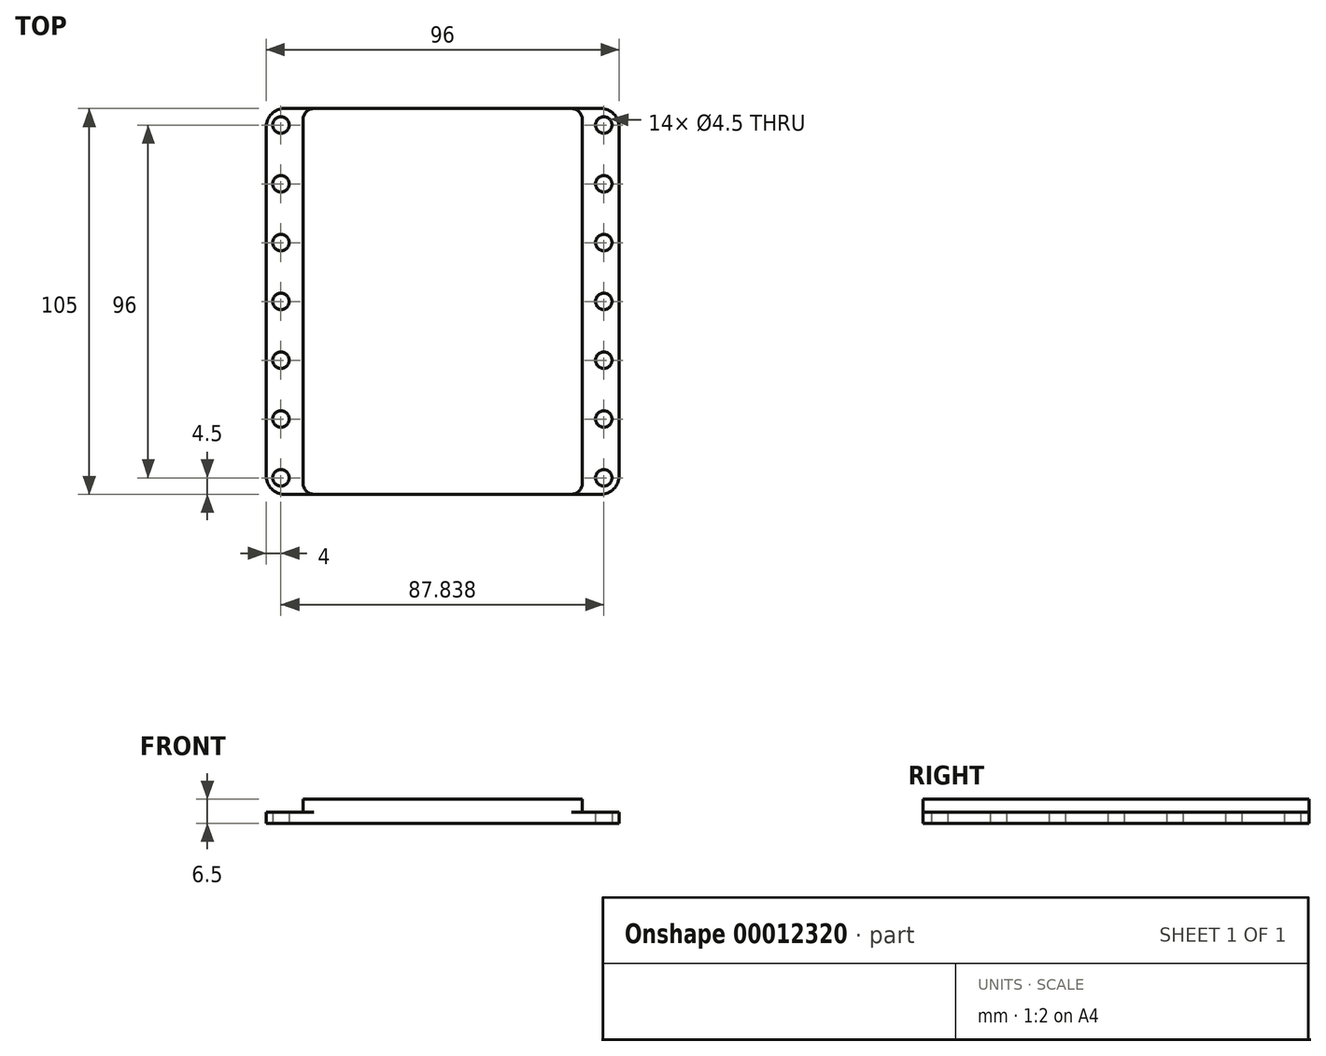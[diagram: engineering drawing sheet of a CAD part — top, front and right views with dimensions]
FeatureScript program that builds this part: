
annotation { "Feature Type Name" : "Feature", "Feature Type Description" : "" }
export const myFeature = defineFeature(function(context is Context, id is Id, definition is map)
    precondition{}
    {
        {
            var Q0;
            Q0=qCreatedBy(makeId("Front.planeOp"),FACE);
            var sketch = newSketch(context, id + "F0", { "sketchPlane" : qUnion([Q0])});
            skLineSegment(sketch, "E0.bottom", {"start": v(0, 0) * mm, "end": v(96, 0) * mm});
            skLineSegment(sketch, "E0.top", {"start": v(0, 3) * mm, "end": v(10, 3) * mm});
            skLineSegment(sketch, "E0.left", {"start": v(0, 0) * mm, "end": v(0, 3) * mm});
            skLineSegment(sketch, "E0.right", {"start": v(96, 0) * mm, "end": v(96, 3) * mm});
            skLineSegment(sketch, "E1.rect.bottom", {"start": v(86, 6.5) * mm, "end": v(10, 6.5) * mm});
            skLineSegment(sketch, "E1.rect.left", {"start": v(86, 6.5) * mm, "end": v(86, 3) * mm});
            skLineSegment(sketch, "E1.rect.right", {"start": v(10, 6.5) * mm, "end": v(10, 3) * mm});
            skPoint(sketch, "E1.rect.middle", {"position": v(48, 3) * mm});
            skLineSegment(sketch, "E2.trimOffspring", {"start": v(86, 3) * mm, "end": v(96, 3) * mm});
            skPoint(sketch, "E3.orphan", {"position": v(86, -0.5) * mm});
            skPoint(sketch, "E4.orphan", {"position": v(10, -0.5) * mm});
            skSolve(sketch);
        }
        {
            var Q0;
            Q0=qSketchRegion(id+"F0",true);
            extrude(context, id + "F1", {"entities" : qUnion([Q0]), "depth" : 105 * mm});
        }
        {
            var Q0;
            Q0=makeQuery(id+"F1.opExtrude","CAP_EDGE",EDGE,{"disambiguationData":[OSD([sQuery(id+"F0.wireOp",EDGE,"E1.rect.left")])],"isStart":false});
            var Q1;
            Q1=makeQuery(id+"F1.opExtrude","CAP_EDGE",EDGE,{"disambiguationData":[OSD([sQuery(id+"F0.wireOp",EDGE,"E1.rect.left")])],"isStart":true});
            var Q2;
            Q2=makeQuery(id+"F1.opExtrude","CAP_EDGE",EDGE,{"disambiguationData":[OSD([sQuery(id+"F0.wireOp",EDGE,"E1.rect.right")])],"isStart":false});
            var Q3;
            Q3=makeQuery(id+"F1.opExtrude","CAP_EDGE",EDGE,{"disambiguationData":[OSD([sQuery(id+"F0.wireOp",EDGE,"E1.rect.right")])],"isStart":true});
            fillet(context, id + "F2", {"entities" : qUnion([Q0, Q1, Q2, Q3]), "radius" : 3 * mm, "tangentPropagation" : true, "allowEdgeOverflow" : false});
        }
        {
            var Q0;
            Q0=makeQuery(id+"F1.opExtrude","CAP_EDGE",EDGE,{"disambiguationData":[OSD([sQuery(id+"F0.wireOp",EDGE,"E0.left")])],"isStart":true});
            var Q1;
            Q1=makeQuery(id+"F1.opExtrude","CAP_EDGE",EDGE,{"disambiguationData":[OSD([sQuery(id+"F0.wireOp",EDGE,"E0.right")])],"isStart":true});
            var Q2;
            Q2=makeQuery(id+"F1.opExtrude","CAP_EDGE",EDGE,{"disambiguationData":[OSD([sQuery(id+"F0.wireOp",EDGE,"E0.right")])],"isStart":false});
            var Q3;
            Q3=makeQuery(id+"F1.opExtrude","CAP_EDGE",EDGE,{"disambiguationData":[OSD([sQuery(id+"F0.wireOp",EDGE,"E0.left")])],"isStart":false});
            fillet(context, id + "F3", {"entities" : qUnion([Q0, Q1, Q2, Q3]), "radius" : 5 * mm, "tangentPropagation" : true, "allowEdgeOverflow" : false});
        }
        {
            var Q0;
            Q0=makeQuery(id+"F1.opExtrude","SWEPT_FACE",FACE,{"disambiguationData":[OSD([sQuery(id+"F0.wireOp",EDGE,"E0.bottom")])]});
            var sketch = newSketch(context, id + "F4", { "sketchPlane" : qUnion([Q0])});
            skLineSegment(sketch, "E5", {"start": v(48, 105) * mm, "end": v(48, 0) * mm, "construction": true});
            skCircle(sketch, "E6", {"center": v(4, 100.5) * mm, "radius": 2.25 * mm});
            skCircle(sketch, "E7.0.1.0", {"center": v(4, 84.5) * mm, "radius": 2.25 * mm});
            skCircle(sketch, "E7.0.2.0", {"center": v(4, 68.5) * mm, "radius": 2.25 * mm});
            skCircle(sketch, "E7.0.3.0", {"center": v(4, 52.5) * mm, "radius": 2.25 * mm});
            skCircle(sketch, "E7.0.4.0", {"center": v(4, 36.5) * mm, "radius": 2.25 * mm});
            skCircle(sketch, "E7.0.5.0", {"center": v(4, 20.5) * mm, "radius": 2.25 * mm});
            skCircle(sketch, "E7.0.6.0", {"center": v(4, 4.5) * mm, "radius": 2.25 * mm});
            skCircle(sketch, "E7.1.0.0", {"center": v(91.84, 100.5) * mm, "radius": 2.25 * mm});
            skCircle(sketch, "E7.1.1.0", {"center": v(91.84, 84.5) * mm, "radius": 2.25 * mm});
            skCircle(sketch, "E7.1.2.0", {"center": v(91.84, 68.5) * mm, "radius": 2.25 * mm});
            skCircle(sketch, "E7.1.3.0", {"center": v(91.84, 52.5) * mm, "radius": 2.25 * mm});
            skCircle(sketch, "E7.1.4.0", {"center": v(91.84, 36.5) * mm, "radius": 2.25 * mm});
            skCircle(sketch, "E7.1.5.0", {"center": v(91.84, 20.5) * mm, "radius": 2.25 * mm});
            skCircle(sketch, "E7.1.6.0", {"center": v(91.84, 4.5) * mm, "radius": 2.25 * mm});
            skLineSegment(sketch, "E7.direction1", {"start": v(4, 100.5) * mm, "end": v(91.84, 100.5) * mm, "construction": true});
            skLineSegment(sketch, "E7.direction2", {"start": v(4, 100.5) * mm, "end": v(4, 84.5) * mm, "construction": true});
            skSolve(sketch);
        }
        {
            var Q0;
            Q0=qSketchRegion(id+"F4",true);
            extrude(context, id + "F5", {"entities" : qUnion([Q0]), "operationType" : NewBodyOperationType.REMOVE, "endBound" : BoundingType.UP_TO_NEXT, "oppositeDirection" : true, "depth" : 25 * mm});
        }
    });
